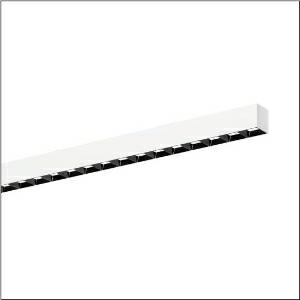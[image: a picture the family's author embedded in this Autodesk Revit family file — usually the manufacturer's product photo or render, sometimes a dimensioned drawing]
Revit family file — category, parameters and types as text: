
# Revit family: silica_21_51mx24tctaw
name_source: partatom
category: Lighting Fixtures
units: mm (PartAtom-declared; Revit-internal decimal feet)

## family parameters
Cut with Voids When Loaded = No
Host = Face
Light Source = No
Part Type = Normal
Room Calculation Point = No
Round Connector Dimension = Use Diameter
Shared = No

## types (1)
- --- (1 x LED, 8200 lm, 81.1 W, 6500K)
    Apparent Load = 81 VA
    CIE Flux Codes = 74 94 99 100 100
    Color Rendering = 80
    Color Temperature = 6500K
    Default Elevation = 1800 mm
    Description = Silica 21, office luminaire, primary light control with darklight reflector, of PMMA, black, light emission: direct distribution, primary light characteristic: asymmetric, installation type: surface-mounted, LED, rated luminous flux: 8.200lm, luminous efficacy: 96lm/W, light colour: 8tw, colour temperature: 2700..6500K, control gear: DALI DT8, with terminal, 3+2-pole, max. 2.5mm², mains connection: 220..240V, AC, 50/60Hz, rated input power: 85.2W, luminaire housing, of aluminium, traffic white (RAL 9016), length: 3.004mm, width: 53mm, height: 53mm, protection rating (complete): IP20, insulation class (complete): insulation class I (protective earthing), certification: CE, permissible operating ambient temperature: 0..+35°C, standard: EN 50419, packaging unit: 1 piece
    Height = 53 mm
    Lamp = 1 x LED
    Lamp Light Flux = 8200 lm
    Lamp Power = 81.1 W
    Lamp count = 1
    Length = 3004 mm
    Luminous efficacy = 101 lm/W
    Manufacturer = Siteco
    ModVariant = No
    Model = 51MX24TCTAW
    Mounting Place = Ceiling
    Mounting Type = Surface mounted
    Number of Poles = 1
    OnlyDefault = Yes
    Power Factor = 1
    Product Name = Silica 21
    Product group = office luminaire | ceiling mounted
    ProductGroupID = 301
    Protection Class = Protection class I
    Protection Degree = IP 20
    RLX_Detail_Level = 1
    RLX_Emergency_Light_Flux = 0 lm
    RLX_Emergency_Type = 0
    RLX_Emergency_Type_DB = No
    RlxData = <blob elided: 58941 chars, md5=cb999434>
    Socket = socket
    Standby Power = 0 W
    System Light Flux = 8200 lm
    System Power = 81 W
    Type Comments = individual setting
    Type Image = l_1335873.jpg
    URL = http://relux.com
    VarID = @adj_139499
    Voltage = 0 V
    Weight = 0.00 kg
    Width = 53 mm

## geometry (parser evidence)
native form markers: Blend x4, Sweep x11
no freeform markers — native parametric forms only
